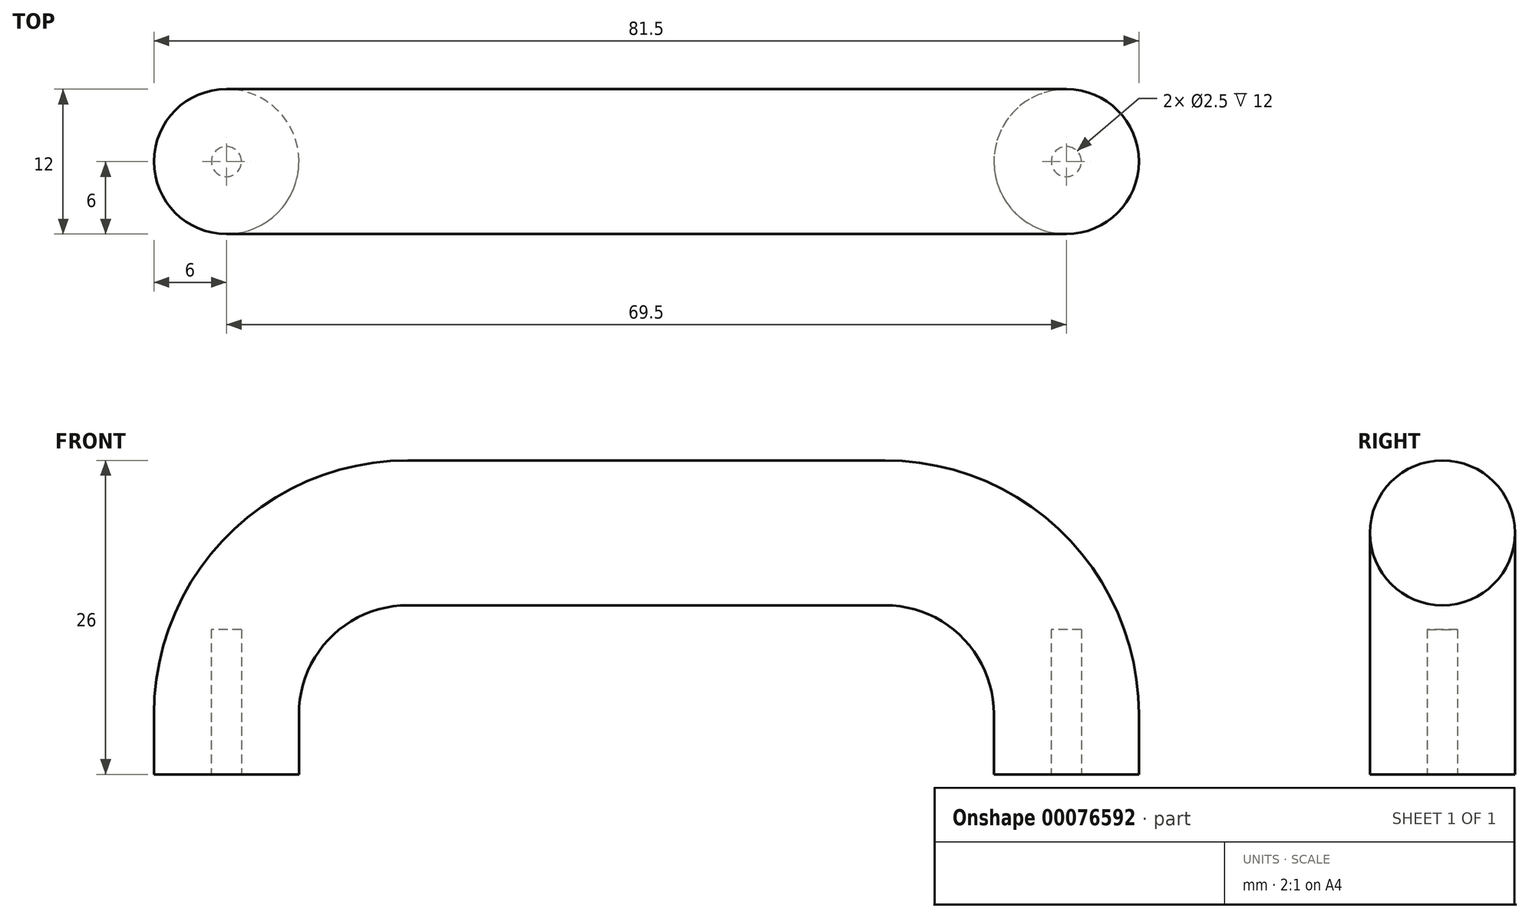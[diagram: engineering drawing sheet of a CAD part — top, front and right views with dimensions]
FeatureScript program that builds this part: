
annotation { "Feature Type Name" : "Feature", "Feature Type Description" : "" }
export const myFeature = defineFeature(function(context is Context, id is Id, definition is map)
    precondition{}
    {
        {
            var Q0;
            Q0=qCreatedBy(makeId("Top.planeOp"),FACE);
            var sketch = newSketch(context, id + "F0", { "sketchPlane" : qUnion([Q0])});
            skCircle(sketch, "E0", {"center": v(0, 0) * mm, "radius": 1.25 * mm});
            skCircle(sketch, "E1", {"center": v(69.5, 0) * mm, "radius": 1.25 * mm});
            skLineSegment(sketch, "E2", {"start": v(0, 0) * mm, "end": v(69.5, 0) * mm});
            skCircle(sketch, "E3", {"center": v(0, 0) * mm, "radius": 6 * mm});
            skCircle(sketch, "E4", {"center": v(69.5, 0) * mm, "radius": 6 * mm});
            skSolve(sketch);
        }
        {
            var Q0;
            Q0=qCreatedBy(makeId("Front.planeOp"),FACE);
            var Q1;
            Q1=qCreatedBy(makeId("Front.planeOp"),FACE);
            var sketch = newSketch(context, id + "F1", { "sketchPlane" : qUnion([Q0, Q1])});
            skLineSegment(sketch, "E5", {"start": v(0, 0) * mm, "end": v(0, 5) * mm});
            skLineSegment(sketch, "E6", {"start": v(15, 20) * mm, "end": v(54.5, 20) * mm});
            skLineSegment(sketch, "E7", {"start": v(69.5, 5) * mm, "end": v(69.5, 0) * mm});
            skPoint(sketch, "E8.visualSharp", {"position": v(0, 20) * mm});
            skArc(sketch, "E8.filletArc", {"start": v(15, 20) * mm, "mid": v(4.4, 15.6) * mm, "end": v(0, 5) * mm});
            skPoint(sketch, "E9.visualSharp", {"position": v(69.5, 20) * mm});
            skArc(sketch, "E9.filletArc", {"start": v(69.5, 5) * mm, "mid": v(65.1, 15.6) * mm, "end": v(54.5, 20) * mm});
            skLineSegment(sketch, "E10", {"start": v(34.75, 20) * mm, "end": v(34.75, 0) * mm, "construction": true});
            skSolve(sketch);
        }
        {
            var Q0;
            Q0=makeQuery(id+"F0.imprint","IMPRINT",FACE,{"disambiguationData":[TD([[makeQuery(id+"F0.imprint","IMPRINT",EDGE,{"derivedFrom":sQuery(id+"F0.wireOp",EDGE,"E0")}),-1.0]])]});
            var Q1;
            Q1=makeQuery(id+"F0.imprint","IMPRINT",FACE,{"disambiguationData":[TD([[makeQuery(id+"F0.imprint","IMPRINT",EDGE,{"derivedFrom":sQuery(id+"F0.wireOp",EDGE,"E0")}),1.0]])]});
            var Q2;
            Q2=sQuery(id+"F1.wireOp",EDGE,"E5");
            var Q3;
            Q3=sQuery(id+"F1.wireOp",EDGE,"E8.filletArc");
            var Q4;
            Q4=sQuery(id+"F1.wireOp",EDGE,"E6");
            var Q5;
            Q5=sQuery(id+"F1.wireOp",EDGE,"E9.filletArc");
            var Q6;
            Q6=sQuery(id+"F1.wireOp",EDGE,"E7");
            sweep(context, id + "F2", {"profiles" : qUnion([Q0, Q1]), "path" : qUnion([Q2, Q3, Q4, Q5, Q6])});
        }
        {
            var Q0;
            Q0=makeQuery(id+"F0.imprint","IMPRINT",FACE,{"disambiguationData":[TD([[makeQuery(id+"F0.imprint","IMPRINT",EDGE,{"derivedFrom":sQuery(id+"F0.wireOp",EDGE,"E0")}),1.0]])]});
            extrude(context, id + "F3", {"entities" : qUnion([Q0]), "operationType" : NewBodyOperationType.REMOVE, "depth" : 12 * mm});
        }
        {
            var Q0;
            Q0=makeQuery(id+"F0.imprint","IMPRINT",FACE,{"disambiguationData":[TD([[makeQuery(id+"F0.imprint","IMPRINT",EDGE,{"derivedFrom":sQuery(id+"F0.wireOp",EDGE,"E1")}),1.0]])]});
            extrude(context, id + "F4", {"entities" : qUnion([Q0]), "operationType" : NewBodyOperationType.REMOVE, "depth" : 12 * mm});
        }
    });
